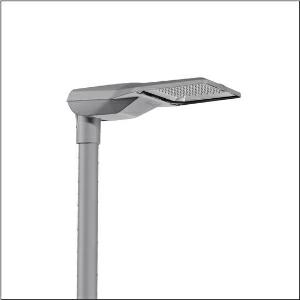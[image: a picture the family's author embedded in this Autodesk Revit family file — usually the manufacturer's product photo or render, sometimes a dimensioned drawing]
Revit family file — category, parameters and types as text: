
# Revit family: streetlight_sl_21_iq_midi___st1_5a_5xe3p31g08mb_98ff
name_source: partatom
category: Lighting Fixtures
units: mm (PartAtom-declared; Revit-internal decimal feet)

## family parameters
Cut with Voids When Loaded = No
Host = Face
Light Source = No
Part Type = Normal
Room Calculation Point = No
Round Connector Dimension = Use Diameter
Shared = No

## types (1)
- --- (1 x LED, 19170 lm, 146.7 W, 3000K)
    Apparent Load = 147 VA
    CIE Flux Codes = 22 53 95 100 100
    Color Rendering = 70
    Color Temperature = 3000K
    Default Elevation = 1800 mm
    Description = Streetlight SL 21 iQ midi, mast luminaire, primary light control with lens, of PMMA, primary optical cover: cover, of toughened safety glass, transparent, light distribution: ST1.5a, light emission: direct distribution, primary light characteristic: asymmetric, installation type: post-top, side-entry, LED, High Power LED, rated luminous flux: 19.170lm, luminous efficacy: 131lm/W, light colour: 730, colour temperature: 3000K, control: Street-Remote, Auto-Match, Temp-Guard, Lumen-Switch, Night-Set, Smart-Wire, Light-Fading, Desk-Remote (wireless, voltage-free reading and setting of iQ features in the workshop via application-optimized NFC function/RFID function), optimised constant luminous flux control (CLO 2.0), presetting dimming linear, mains connection: 230..240V, AC, 50/60Hz, start of lifetime: 147W, end of service life: 161W, reduction: 62W, luminaire housing, of diecast aluminium, powder-coated, Siteco® metallic grey (DB 702S), corrosivity category C5 mid according to DIN EN ISO 12944, please order mast flange separately, inclination adjustable: 0°, 5°, 10°, 15°, sealing non-destructively replaceable, multi-level sealing system, length: 644mm, width: 335mm, height: 110mm, mast flange for spigot size: 42mm (side-entry): 5XC10008XM4, 60/48mm (side-entry/post-top): 5XC10108XM2, 76/60mm (side-entry/post-top): 5XC10108XM1, protection rating (complete): IP66, insulation class (complete): insulation class II (safety insulation), certification: CE, ENEC, ENEC+, VDE, impact resistance: IK09, permissible operating ambient temperature for outdoor applications: -40..+50°C, standard-compliant lighting for roads and squares, packaging unit: 1 piece

Light Distribution: ST1.5a
    Height = 111 mm
    Lamp = 1 x LED
    Lamp Light Flux = 19170 lm
    Lamp Power = 146.7 W
    Lamp count = 1
    Length = 644 mm
    Luminous efficacy = 131 lm/W
    Manufacturer = Siteco
    ModVariant = No
    Model = 5XE3P31G08MB
    Number of Poles = 1
    OnlyDefault = Yes
    Power Factor = 1
    Product Name = Streetlight SL 21 iQ midi | ST1.5a
    Product group = mast luminaire | pylon top
    ProductGroupID = 6100
    Protection Class = Protection class II
    Protection Degree = IP 66
    RLX_Detail_Level = 1
    RLX_Emergency_Light_Flux = 0 lm
    RLX_Emergency_Type = 0
    RLX_Emergency_Type_DB = No
    RlxData = <blob elided: 94521 chars, md5=9c5894d0>
    Socket = socket
    Standby Power = 0 W
    System Light Flux = 19169 lm
    System Power = 147 W
    Type Comments = factory setting: luminous flux: 100 % | dim-lin: 254 | 753 mA
    Type Image = l_1004298.jpg
    URL = http://relux.com
    VarID = @adj_109661
    Voltage = 0 V
    Weight = 0.00 kg
    Width = 336 mm

## geometry (parser evidence)
native form markers: Blend x4, Sweep x9
no freeform markers — native parametric forms only
